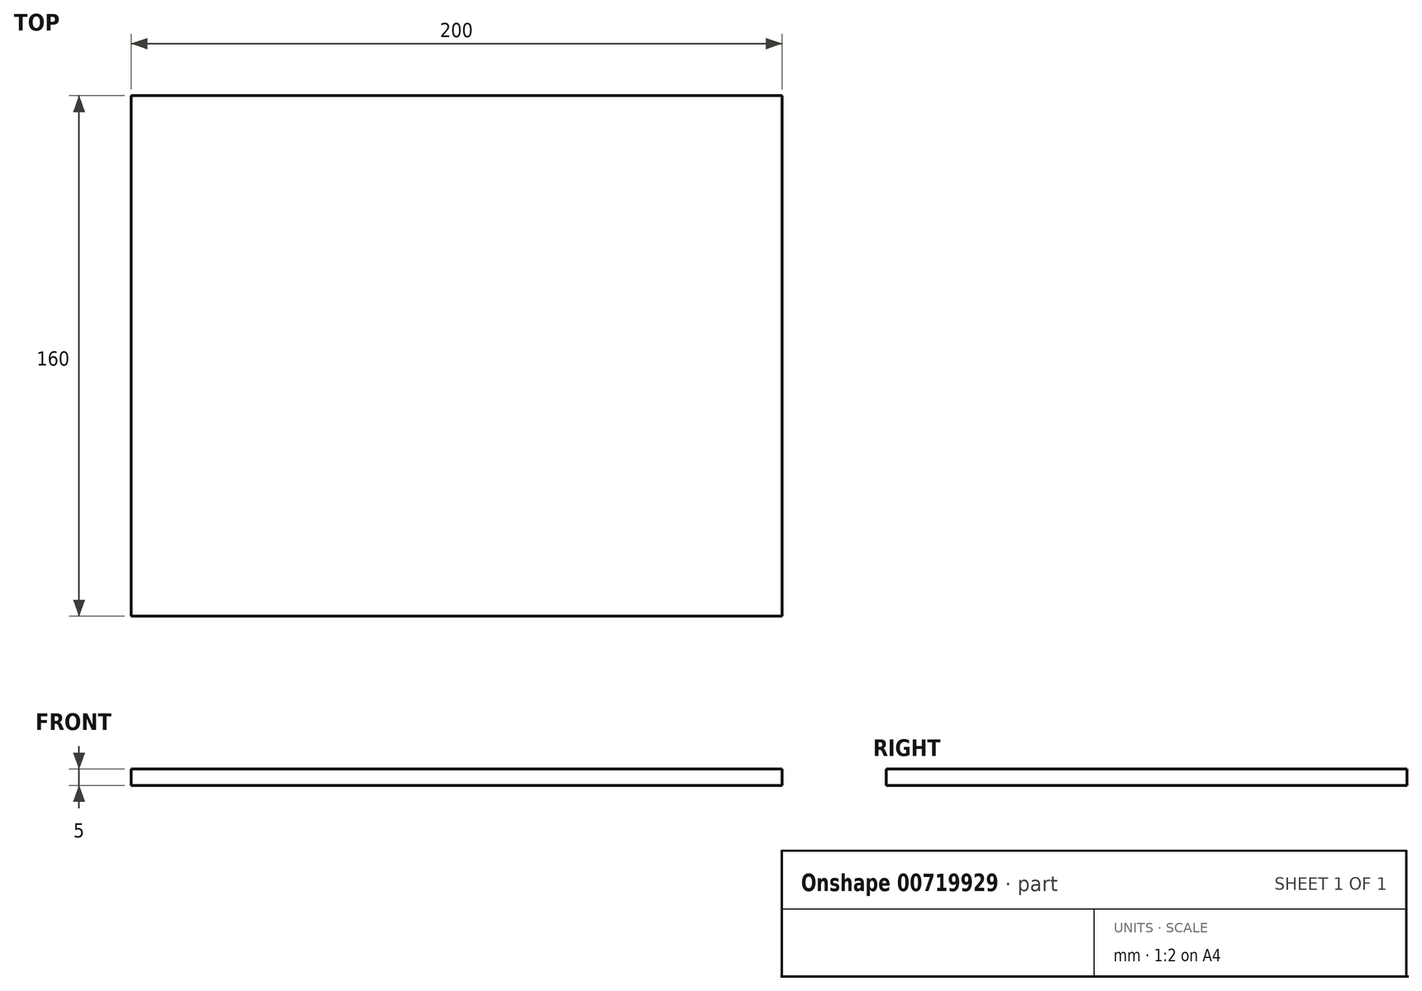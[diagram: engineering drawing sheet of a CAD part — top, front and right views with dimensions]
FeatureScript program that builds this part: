
annotation { "Feature Type Name" : "Feature", "Feature Type Description" : "" }
export const myFeature = defineFeature(function(context is Context, id is Id, definition is map)
    precondition{}
    {
        {
            var Q0;
            Q0=qCreatedBy(makeId("Top.planeOp"),FACE);
            var sketch = newSketch(context, id + "F0", { "sketchPlane" : qUnion([Q0])});
            skLineSegment(sketch, "E0.bottom", {"start": v(-200, 160) * mm, "end": v(0, 160) * mm});
            skLineSegment(sketch, "E0.top", {"start": v(-200, 0) * mm, "end": v(0, 0) * mm});
            skLineSegment(sketch, "E0.left", {"start": v(-200, 160) * mm, "end": v(-200, 0) * mm});
            skLineSegment(sketch, "E0.right", {"start": v(0, 160) * mm, "end": v(0, 0) * mm});
            skSolve(sketch);
        }
        {
            var Q0;
            Q0 = qSketchRegion(id + "F0", true);
            extrude(context, id + "F1", {"entities" : qUnion([Q0]), "depth" : 5 * mm, "offsetDistance" : 25 * mm});
        }
    });
